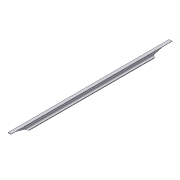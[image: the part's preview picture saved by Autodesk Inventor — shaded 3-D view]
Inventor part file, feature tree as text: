
AUTODESK INVENTOR PART (.ipt)
format: ipt  version: 2012 (Build 160160000, 160)  size: 156,160 bytes
history: native  units: in
note: dims shown in document units (in); Inventor stores cm internally (conversion verified against a paired STEP export)
features: extrude x3, sketch x3, hole x1, pattern_linear x1, plane x1, mirror x1
ambient origin geometry x8: Origin, YZ Plane, XZ Plane, XY Plane, X Axis, Y Axis, Z Axis, Center Point
bodies: Solid1 (feature_tree)
feature tree (10):
  extrude  "Extrusion1"  Depth=3.0in
  extrude  "Extrusion2"  Depth=2.75in
  extrude  "Extrusion3"  Depth=12.0in TaperAngle=0.0deg
  hole  "Hole1"  [1 undecoded]
  pattern_linear  "Rectangular Pattern1"  Spacing1=1.5in  [1 undecoded]
  plane  "Work Plane1"
  mirror  "Mirror1"
  sketch  "Sketch1"  dims[d4=82.0in d5=0.0in d15=3.0in]
  sketch  "Sketch2"  dims[d16=2.75in d19=9.5in d20=2.75in]
  sketch  "Sketch3"  dims[d21=9.5in d22=12.0in d23=0.0in d25=0.258in d26=1.5in d28=0.258in d29=0.1in d30=0.27in d31=2.75in d32=1.0in d33=1.375in d34=0.125in d35=66.0in d36=8.0in d37=1.25in d38=0.0625in d39=6.6929in d41=4.0in d42=0.3937in d44=1.0in d46=7.5in d47=1.5in d48=0.375in d49=1.0in d50=0.0in d51=11.0in d52=1.5in d53=0.1406in d54=0.75in d55=0.375in d56=0.25in d57=0.5635in d58=1.0in d59=0.8108in d60=0.7874in d62=28.0in d63=33.0in]
note: 2 required parameter values undecoded (feature->parameter linkage not recoverable at this tier; creation-order binding heuristic only, values carry confidence <= 0.55)
